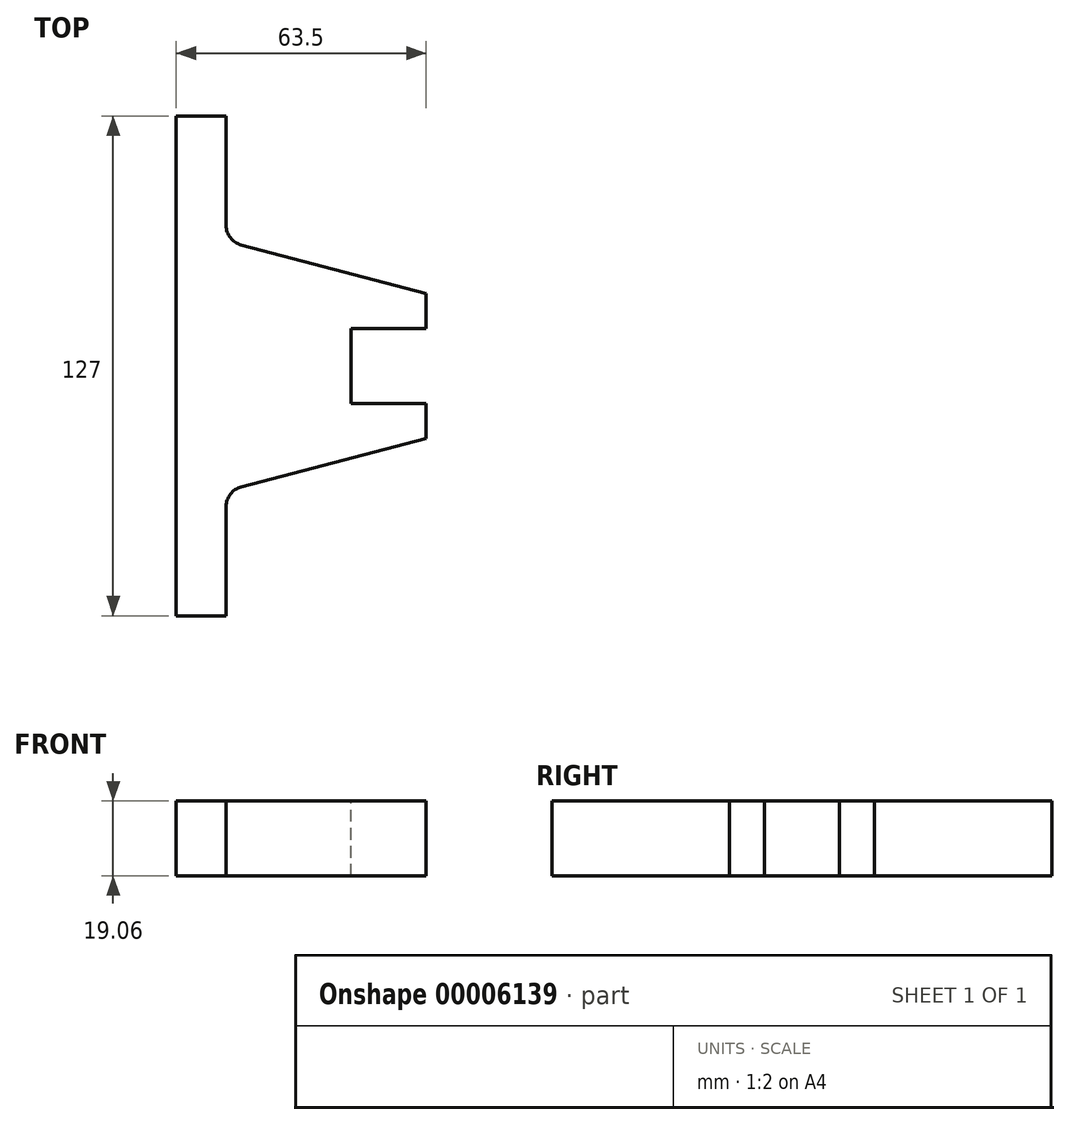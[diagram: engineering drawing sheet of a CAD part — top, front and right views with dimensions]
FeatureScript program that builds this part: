
annotation { "Feature Type Name" : "Feature", "Feature Type Description" : "" }
export const myFeature = defineFeature(function(context is Context, id is Id, definition is map)
    precondition{}
    {
        {
            var Q0;
            Q0=qCreatedBy(makeId("Top.planeOp"),FACE);
            var sketch = newSketch(context, id + "F0", { "sketchPlane" : qUnion([Q0])});
            skLineSegment(sketch, "E0.bottom", {"start": v(-31.75, 63.5) * mm, "end": v(31.75, 63.5) * mm});
            skLineSegment(sketch, "E0.top", {"start": v(-31.75, -63.5) * mm, "end": v(31.75, -63.5) * mm});
            skLineSegment(sketch, "E0.left", {"start": v(-31.75, 63.5) * mm, "end": v(-31.75, -63.5) * mm});
            skLineSegment(sketch, "E0.right", {"start": v(31.75, 63.5) * mm, "end": v(31.75, -63.5) * mm});
            skLineSegment(sketch, "E1", {"start": v(31.75, 63.5) * mm, "end": v(-31.75, -63.5) * mm, "construction": true});
            skSolve(sketch);
        }
        {
            var Q0;
            Q0 = qSketchRegion(id + "F0", true);
            extrude(context, id + "F1", {"entities" : qUnion([Q0]), "endBound" : BoundingType.SYMMETRIC, "depth" : 19.05 * mm});
        }
        {
            var Q0;
            Q0=makeQuery(id+"F1.opExtrude","CAP_FACE",FACE,{"disambiguationData":[OSD([sQuery(id+"F0.wireOp",EDGE,"E0.bottom"),sQuery(id+"F0.wireOp",EDGE,"E0.top"),sQuery(id+"F0.wireOp",EDGE,"E0.left"),sQuery(id+"F0.wireOp",EDGE,"E0.right")])],"isStart":false});
            var sketch = newSketch(context, id + "F2", { "sketchPlane" : qUnion([Q0])});
            skLineSegment(sketch, "E2", {"start": v(0, 0) * mm, "end": v(31.75, 0) * mm, "construction": true});
            skLineSegment(sketch, "E3.bottom", {"start": v(31.75, 9.53) * mm, "end": v(12.7, 9.53) * mm});
            skLineSegment(sketch, "E3.top", {"start": v(31.75, -9.53) * mm, "end": v(12.7, -9.53) * mm});
            skLineSegment(sketch, "E3.left", {"start": v(31.75, 9.53) * mm, "end": v(31.75, -9.53) * mm});
            skLineSegment(sketch, "E3.right", {"start": v(12.7, 9.53) * mm, "end": v(12.7, -9.53) * mm});
            skSolve(sketch);
        }
        {
            var Q0;
            Q0 = qSketchRegion(id + "F2", true);
            extrude(context, id + "F3", {"entities" : qUnion([Q0]), "operationType" : NewBodyOperationType.REMOVE, "endBound" : BoundingType.THROUGH_ALL, "oppositeDirection" : true, "depth" : 25.4 * mm});
        }
        {
            var Q0;
            Q0=makeQuery(id+"F1.opExtrude","CAP_FACE",FACE,{"disambiguationData":[OSD([sQuery(id+"F0.wireOp",EDGE,"E0.bottom"),sQuery(id+"F0.wireOp",EDGE,"E0.top"),sQuery(id+"F0.wireOp",EDGE,"E0.left"),sQuery(id+"F0.wireOp",EDGE,"E0.right")])],"isStart":false});
            var sketch = newSketch(context, id + "F4", { "sketchPlane" : qUnion([Q0])});
            skLineSegment(sketch, "E4", {"start": v(-19.05, 63.5) * mm, "end": v(-19.05, 31.75) * mm});
            skLineSegment(sketch, "E5", {"start": v(-19.05, 31.75) * mm, "end": v(31.75, 18.41) * mm});
            skLineSegment(sketch, "E6", {"start": v(-19.05, -31.75) * mm, "end": v(31.75, -18.42) * mm});
            skLineSegment(sketch, "E7.trimOffspring", {"start": v(-19.05, -31.75) * mm, "end": v(-19.05, -63.5) * mm});
            skLineSegment(sketch, "E8", {"start": v(-19.05, 31.75) * mm, "end": v(-19.05, -31.75) * mm, "construction": true});
            skLineSegment(sketch, "E9", {"start": v(31.75, 18.41) * mm, "end": v(31.75, -18.41) * mm, "construction": true});
            skLineSegment(sketch, "E10", {"start": v(31.75, 0) * mm, "end": v(-19.05, 0) * mm, "construction": true});
            skLineSegment(sketch, "E11", {"start": v(-19.05, 63.5) * mm, "end": v(31.75, 63.5) * mm});
            skLineSegment(sketch, "E12", {"start": v(31.75, 63.5) * mm, "end": v(31.75, 18.42) * mm});
            skLineSegment(sketch, "E13", {"start": v(-19.05, -63.5) * mm, "end": v(31.75, -63.5) * mm});
            skLineSegment(sketch, "E14", {"start": v(31.75, -63.5) * mm, "end": v(31.75, -18.42) * mm});
            skSolve(sketch);
        }
        {
            var Q0;
            Q0 = qSketchRegion(id + "F4", true);
            extrude(context, id + "F5", {"entities" : qUnion([Q0]), "operationType" : NewBodyOperationType.REMOVE, "endBound" : BoundingType.THROUGH_ALL, "oppositeDirection" : true, "depth" : 25.4 * mm});
        }
        {
            var Q0;
            Q0=makeQuery(id+"F5.boolean.opBoolean","COPY",EDGE,{"derivedFrom":makeQuery(id+"F5.opExtrude","SWEPT_EDGE",EDGE,{"disambiguationData":[OSD([sQuery(id+"F4.wireOp",EDGE,"E6"),sQuery(id+"F4.wireOp",EDGE,"E7.trimOffspring")])]})});
            var Q1;
            Q1=makeQuery(id+"F5.boolean.opBoolean","COPY",EDGE,{"derivedFrom":makeQuery(id+"F5.opExtrude","SWEPT_EDGE",EDGE,{"disambiguationData":[OSD([sQuery(id+"F0.wireOp",EDGE,"E0.top"),sQuery(id+"F4.wireOp",EDGE,"E7.trimOffspring"),sQuery(id+"F4.wireOp",EDGE,"E13")])]})});
            var Q2;
            Q2=makeQuery(id+"F5.boolean.opBoolean","COPY",EDGE,{"derivedFrom":makeQuery(id+"F5.opExtrude","SWEPT_EDGE",EDGE,{"disambiguationData":[OSD([sQuery(id+"F0.wireOp",EDGE,"E0.right"),sQuery(id+"F4.wireOp",EDGE,"E6"),sQuery(id+"F4.wireOp",EDGE,"E14")])]})});
            var Q3;
            Q3=makeQuery(id+"F5.boolean.opBoolean","COPY",EDGE,{"derivedFrom":makeQuery(id+"F5.opExtrude","SWEPT_EDGE",EDGE,{"disambiguationData":[OSD([sQuery(id+"F0.wireOp",EDGE,"E0.right"),sQuery(id+"F4.wireOp",EDGE,"E5"),sQuery(id+"F4.wireOp",EDGE,"E12")])]})});
            var Q4;
            Q4=makeQuery(id+"F5.boolean.opBoolean","COPY",EDGE,{"derivedFrom":makeQuery(id+"F5.opExtrude","SWEPT_EDGE",EDGE,{"disambiguationData":[OSD([sQuery(id+"F4.wireOp",EDGE,"E4"),sQuery(id+"F4.wireOp",EDGE,"E5")])]})});
            var Q5;
            Q5=makeQuery(id+"F5.boolean.opBoolean","COPY",EDGE,{"derivedFrom":makeQuery(id+"F5.opExtrude","SWEPT_EDGE",EDGE,{"disambiguationData":[OSD([sQuery(id+"F0.wireOp",EDGE,"E0.bottom"),sQuery(id+"F4.wireOp",EDGE,"E4"),sQuery(id+"F4.wireOp",EDGE,"E11")])]})});
            fillet(context, id + "F6", {"entities" : qUnion([Q0, Q1, Q2, Q3, Q4, Q5]), "radius" : 5.08 * mm, "tangentPropagation" : true, "allowEdgeOverflow" : false});
        }
    });
